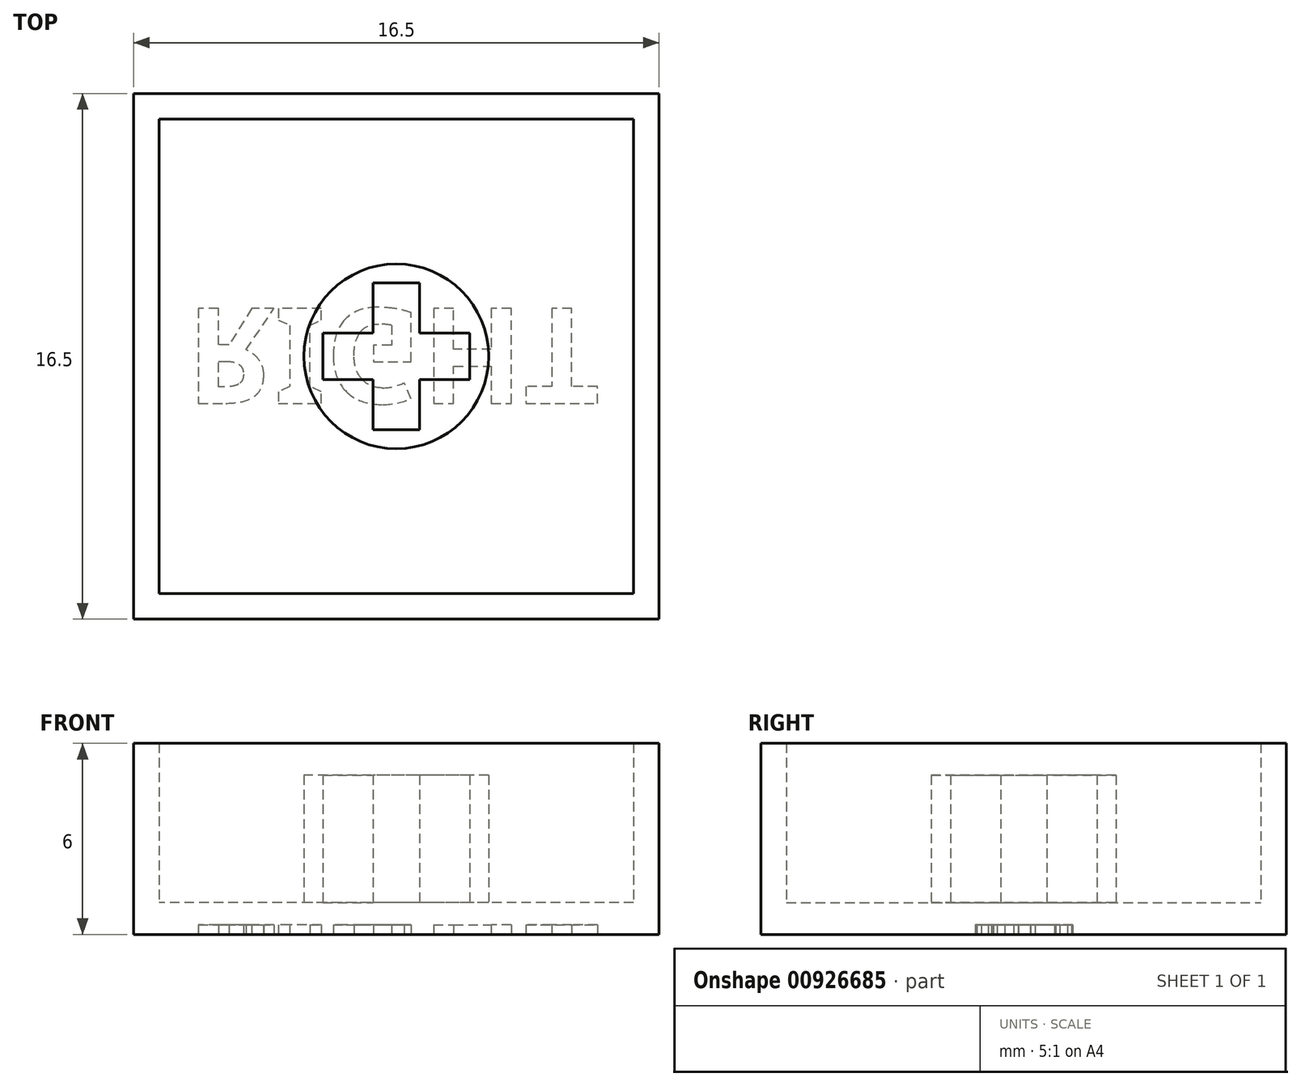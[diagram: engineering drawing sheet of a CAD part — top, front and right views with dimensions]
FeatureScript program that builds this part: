
annotation { "Feature Type Name" : "Feature", "Feature Type Description" : "" }
export const myFeature = defineFeature(function(context is Context, id is Id, definition is map)
    precondition{}
    {
        {
            var Q0;
            Q0=qCreatedBy(makeId("Top.planeOp"),FACE);
            var sketch = newSketch(context, id + "F0", { "sketchPlane" : qUnion([Q0])});
            skLineSegment(sketch, "E0.bottom", {"start": v(0, 0) * mm, "end": v(-16.5, 0) * mm});
            skLineSegment(sketch, "E0.top", {"start": v(0, 16.5) * mm, "end": v(-16.5, 16.5) * mm});
            skLineSegment(sketch, "E0.left", {"start": v(0, 0) * mm, "end": v(0, 16.5) * mm});
            skLineSegment(sketch, "E0.right", {"start": v(-16.5, 0) * mm, "end": v(-16.5, 16.5) * mm});
            skSolve(sketch);
        }
        {
            var Q0;
            Q0=makeQuery(id+"F0.imprint","IMPRINT",FACE,{"disambiguationData":[TD([[makeQuery(id+"F0.imprint","IMPRINT",EDGE,{"derivedFrom":sQuery(id+"F0.wireOp",EDGE,"E0.bottom")}),-1.0]])]});
            extrude(context, id + "F1", {"entities" : qUnion([Q0]), "depth" : 1 * mm, "offsetDistance" : 25 * mm});
        }
        {
            var Q0;
            Q0=makeQuery(id+"F1.opExtrude","CAP_FACE",FACE,{"disambiguationData":[OSD([sQuery(id+"F0.wireOp",EDGE,"E0.bottom"),sQuery(id+"F0.wireOp",EDGE,"E0.top"),sQuery(id+"F0.wireOp",EDGE,"E0.left"),sQuery(id+"F0.wireOp",EDGE,"E0.right")])],"isStart":false});
            var sketch = newSketch(context, id + "F2", { "sketchPlane" : qUnion([Q0])});
            skLineSegment(sketch, "E1.bottom", {"start": v(-11.15, 11.15) * mm, "end": v(-5.35, 11.15) * mm});
            skLineSegment(sketch, "E1.top", {"start": v(-11.15, 5.35) * mm, "end": v(-5.35, 5.35) * mm});
            skLineSegment(sketch, "E1.left", {"start": v(-11.15, 11.15) * mm, "end": v(-11.15, 5.35) * mm});
            skLineSegment(sketch, "E1.right", {"start": v(-5.35, 11.15) * mm, "end": v(-5.35, 5.35) * mm});
            skLineSegment(sketch, "E2", {"start": v(-11.15, 11.15) * mm, "end": v(-11.15, 16.5) * mm});
            skLineSegment(sketch, "E3", {"start": v(-11.15, 5.35) * mm, "end": v(-11.15, 0) * mm});
            skLineSegment(sketch, "E4", {"start": v(-11.15, 11.15) * mm, "end": v(-16.5, 11.15) * mm});
            skLineSegment(sketch, "E5", {"start": v(-5.35, 11.15) * mm, "end": v(0, 11.15) * mm});
            skLineSegment(sketch, "E6", {"start": v(-8.98, 10.55) * mm, "end": v(-7.53, 10.55) * mm});
            skLineSegment(sketch, "E7", {"start": v(-7.53, 10.55) * mm, "end": v(-7.53, 8.98) * mm});
            skLineSegment(sketch, "E8", {"start": v(-7.53, 8.98) * mm, "end": v(-5.95, 8.98) * mm});
            skLineSegment(sketch, "E9", {"start": v(-5.95, 8.98) * mm, "end": v(-5.95, 7.53) * mm});
            skLineSegment(sketch, "E10", {"start": v(-5.95, 7.53) * mm, "end": v(-7.53, 7.53) * mm});
            skLineSegment(sketch, "E11", {"start": v(-7.53, 7.53) * mm, "end": v(-7.53, 5.95) * mm});
            skLineSegment(sketch, "E12", {"start": v(-7.53, 5.95) * mm, "end": v(-8.98, 5.95) * mm});
            skLineSegment(sketch, "E13", {"start": v(-8.98, 5.95) * mm, "end": v(-8.98, 7.53) * mm});
            skLineSegment(sketch, "E14", {"start": v(-8.98, 7.53) * mm, "end": v(-10.55, 7.53) * mm});
            skLineSegment(sketch, "E15", {"start": v(-10.55, 7.53) * mm, "end": v(-10.55, 8.98) * mm});
            skLineSegment(sketch, "E16", {"start": v(-10.55, 8.98) * mm, "end": v(-8.98, 8.98) * mm});
            skLineSegment(sketch, "E17", {"start": v(-8.98, 8.98) * mm, "end": v(-8.98, 10.55) * mm});
            skLineSegment(sketch, "E18", {"start": v(-8.98, 10.55) * mm, "end": v(-8.98, 11.15) * mm});
            skLineSegment(sketch, "E19", {"start": v(-8.98, 5.95) * mm, "end": v(-8.98, 5.35) * mm});
            skLineSegment(sketch, "E20", {"start": v(-8.98, 10.55) * mm, "end": v(-11.15, 10.55) * mm});
            skLineSegment(sketch, "E21", {"start": v(-7.53, 10.55) * mm, "end": v(-5.35, 10.55) * mm});
            skLineSegment(sketch, "E22", {"start": v(-11.15, 9.8) * mm, "end": v(-9.67, 11.15) * mm});
            skPoint(sketch, "E23", {"position": v(-8.25, 8.25) * mm});
            skPoint(sketch, "E23.positionSnap0", {"position": v(-5.35, 8.25) * mm});
            skPoint(sketch, "E23.positionSnap1", {"position": v(-8.25, 11.15) * mm});
            skLineSegment(sketch, "E24", {"start": v(-11.15, 6.3) * mm, "end": v(-9.39, 5.35) * mm});
            skLineSegment(sketch, "E25", {"start": v(-7.11, 5.35) * mm, "end": v(-5.35, 6.3) * mm});
            skLineSegment(sketch, "E26", {"start": v(-5.35, 9.55) * mm, "end": v(-6.55, 11.15) * mm});
            skCircle(sketch, "E27", {"center": v(-8.25, 8.25) * mm, "radius": 2.9 * mm});
            skSolve(sketch);
        }
        {
            var Q0;
            Q0=makeQuery(id+"F2.imprint","IMPRINT",FACE,{"disambiguationData":[TD([[makeQuery(id+"F2.imprint","IMPRINT",EDGE,{"derivedFrom":sQuery(id+"F2.wireOp",EDGE,"E13")}),1.0]])]});
            var Q1;
            Q1=makeQuery(id+"F2.imprint","IMPRINT",FACE,{"disambiguationData":[TD([[makeQuery(id+"F2.imprint","IMPRINT",EDGE,{"derivedFrom":sQuery(id+"F2.wireOp",EDGE,"E7")}),1.0]])]});
            var Q2;
            Q2=makeQuery(id+"F2.imprint","IMPRINT",FACE,{"disambiguationData":[TD([[makeQuery(id+"F2.imprint","IMPRINT",EDGE,{"derivedFrom":sQuery(id+"F2.wireOp",EDGE,"E6")}),1.0]])]});
            var Q3;
            {var subQ3=sQuery(id+"F2.wireOp",EDGE,"E18");Q3=makeQuery(id+"F2.imprint","IMPRINT",FACE,{"disambiguationData":[TD([[makeQuery(id+"F2.imprint","IMPRINT",EDGE,{"derivedFrom":subQ3}),1.0]])]});}
            extrude(context, id + "F3", {"entities" : qUnion([Q0, Q1, Q2, Q3]), "operationType" : NewBodyOperationType.ADD, "depth" : 4 * mm, "offsetDistance" : 25 * mm});
        }
        {
            var Q0;
            Q0=makeQuery(id+"F1.opExtrude","CAP_FACE",FACE,{"disambiguationData":[OSD([sQuery(id+"F0.wireOp",EDGE,"E0.bottom"),sQuery(id+"F0.wireOp",EDGE,"E0.top"),sQuery(id+"F0.wireOp",EDGE,"E0.left"),sQuery(id+"F0.wireOp",EDGE,"E0.right")])],"isStart":true});
            var sketch = newSketch(context, id + "F4", { "sketchPlane" : qUnion([Q0])});
            skText(sketch, "E28", { "text": "RIGHT", "fontName": "NotoSans-Bold.ttf"});
            skLineSegment(sketch, "E29", {"start": v(-14.84, -6.75) * mm, "end": v(-14.84, 0) * mm});
            skLineSegment(sketch, "E30", {"start": v(-14.84, -9.75) * mm, "end": v(-14.84, -16.5) * mm});
            skLineSegment(sketch, "E31", {"start": v(-14.84, -6.75) * mm, "end": v(-16.5, -6.75) * mm});
            skLineSegment(sketch, "E32", {"start": v(-1.66, -6.75) * mm, "end": v(0, -6.75) * mm});
            const initialGuessF4  = {"E28": [-0.01484, -0.00975, 1, 0, 0.003]};
            skSetInitialGuess(sketch, initialGuessF4);
            skSolve(sketch);
        }
        {
            var Q0;
            Q0=makeQuery(id+"F4.imprint","IMPRINT",FACE,{"disambiguationData":[TD([[makeQuery(id+"F4.imprint","IMPRINT",EDGE,{"derivedFrom":sQuery(id+"F4.wireOp",EDGE,"E28.sketch_text.stroke-0")}),-1.0]])]});
            var Q1;
            Q1=makeQuery(id+"F4.imprint","IMPRINT",FACE,{"disambiguationData":[TD([[makeQuery(id+"F4.imprint","IMPRINT",EDGE,{"derivedFrom":sQuery(id+"F4.wireOp",EDGE,"E28.sketch_text.stroke-15")}),-1.0]])]});
            var Q2;
            Q2=makeQuery(id+"F4.imprint","IMPRINT",FACE,{"disambiguationData":[TD([[makeQuery(id+"F4.imprint","IMPRINT",EDGE,{"derivedFrom":sQuery(id+"F4.wireOp",EDGE,"E28.sketch_text.stroke-26")}),-1.0]])]});
            var Q3;
            Q3=makeQuery(id+"F4.imprint","IMPRINT",FACE,{"disambiguationData":[TD([[makeQuery(id+"F4.imprint","IMPRINT",EDGE,{"derivedFrom":sQuery(id+"F4.wireOp",EDGE,"E28.sketch_text.stroke-50")}),-1.0]])]});
            var Q4;
            Q4=makeQuery(id+"F4.imprint","IMPRINT",FACE,{"disambiguationData":[TD([[makeQuery(id+"F4.imprint","IMPRINT",EDGE,{"derivedFrom":sQuery(id+"F4.wireOp",EDGE,"E28.sketch_text.stroke-28")}),-1.0]])]});
            var Q5;
            Q5=makeQuery(id+"F4.imprint","IMPRINT",FACE,{"disambiguationData":[TD([[makeQuery(id+"F4.imprint","IMPRINT",EDGE,{"derivedFrom":sQuery(id+"F4.wireOp",EDGE,"E28.sketch_text.stroke-31")}),-1.0]])]});
            var Q6;
            Q6=makeQuery(id+"F4.imprint","IMPRINT",FACE,{"disambiguationData":[TD([[makeQuery(id+"F4.imprint","IMPRINT",EDGE,{"derivedFrom":sQuery(id+"F4.wireOp",EDGE,"E28.sketch_text.stroke-62")}),-1.0]])]});
            extrude(context, id + "F5", {"entities" : qUnion([Q0, Q1, Q2, Q3, Q4, Q5, Q6]), "operationType" : NewBodyOperationType.REMOVE, "oppositeDirection" : true, "depth" : 0.3 * mm, "offsetDistance" : 25 * mm});
        }
        {
            var Q0;
            {var subQ0=sQuery(id+"F0.wireOp",EDGE,"E0.left");var subQ1=sQuery(id+"F0.wireOp",EDGE,"E0.top");var subQ2=sQuery(id+"F0.wireOp",EDGE,"E0.right");var subQ3=sQuery(id+"F0.wireOp",EDGE,"E0.bottom");Q0=makeQuery(id+"F3.boolean.opBoolean","SPLIT",FACE,{"disambiguationData":[TD([makeQuery(id+"F1.opExtrude","SWEPT_FACE",FACE,{"disambiguationData":[OSD([subQ3])]})])],"derivedFrom":makeQuery(id+"F1.opExtrude","CAP_FACE",FACE,{"disambiguationData":[OSD([subQ3,subQ1,subQ0,subQ2])],"isStart":false})});}
            var sketch = newSketch(context, id + "F6", { "sketchPlane" : qUnion([Q0])});
            skLineSegment(sketch, "E33.bottom", {"start": v(0, 0) * mm, "end": v(-16.5, 0) * mm});
            skLineSegment(sketch, "E33.top", {"start": v(0, 16.5) * mm, "end": v(-16.5, 16.5) * mm});
            skLineSegment(sketch, "E33.left", {"start": v(0, 0) * mm, "end": v(0, 16.5) * mm});
            skLineSegment(sketch, "E33.right", {"start": v(-16.5, 0) * mm, "end": v(-16.5, 16.5) * mm});
            skLineSegment(sketch, "E34.0", {"start": v(-0.8, 15.7) * mm, "end": v(-15.7, 15.7) * mm});
            skLineSegment(sketch, "E34.1", {"start": v(-0.8, 0.8) * mm, "end": v(-0.8, 15.7) * mm});
            skLineSegment(sketch, "E34.2", {"start": v(-0.8, 0.8) * mm, "end": v(-15.7, 0.8) * mm});
            skLineSegment(sketch, "E34.3", {"start": v(-15.7, 0.8) * mm, "end": v(-15.7, 15.7) * mm});
            skSolve(sketch);
        }
        {
            var Q0;
            Q0=makeQuery(id+"F6.imprint","IMPRINT",FACE,{"disambiguationData":[TD([[makeQuery(id+"F6.imprint","IMPRINT",EDGE,{"derivedFrom":sQuery(id+"F6.wireOp",EDGE,"E33.bottom")}),-1.0]])]});
            extrude(context, id + "F7", {"entities" : qUnion([Q0]), "operationType" : NewBodyOperationType.ADD, "depth" : 5 * mm, "offsetDistance" : 25 * mm});
        }
    });
